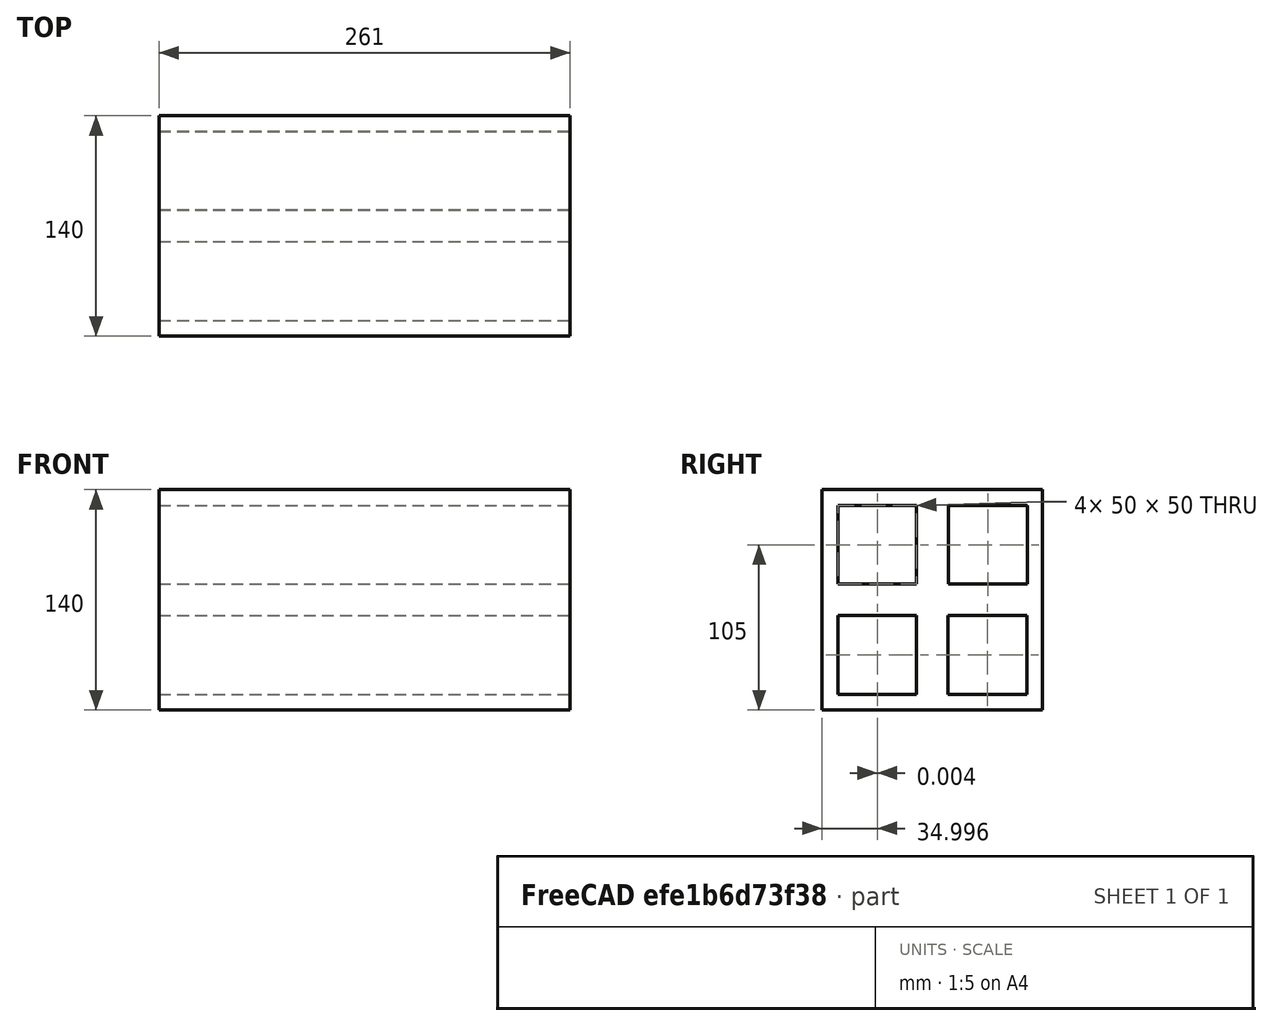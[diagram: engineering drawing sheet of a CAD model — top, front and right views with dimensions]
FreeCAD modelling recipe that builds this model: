
FCSTD DOCUMENT  (FreeCAD 0.21R33694 (Git))
Label: OJT1_T19R01_totxo
License: All rights reserved
LicenseURL: https://en.wikipedia.org/wiki/All_rights_reserved
objects: Sketcher::SketchObject×1, PartDesign::Pad×1, PartDesign::Body×1
note: 4 computed .brp shape members not serialized (recipe doc carries the construction recipe); baked Part::Feature solids carry a one-line shape summary decoded from their .brp

FEATURE [Sketcher::SketchObject] Sketch
  FullyConstrained = false
  MapMode = 5
  Placement = pos=(0,0,0) rot=(0.57735,0.57735,0.57735;2.0944rad)
  Support = -> [YZ_Plane]
  sketch-geometry (20):
    g0: LineSegment StartX=-70 StartY=70 StartZ=0 EndX=70 EndY=70 EndZ=0
    g1: LineSegment StartX=70 StartY=70 StartZ=0 EndX=70 EndY=-70 EndZ=0
    g2: LineSegment StartX=70 StartY=-70 StartZ=0 EndX=-70 EndY=-70 EndZ=0
    g3: LineSegment StartX=-70 StartY=-70 StartZ=0 EndX=-70 EndY=70 EndZ=0
    g4: LineSegment StartX=-60.0035 StartY=60 StartZ=0 EndX=-10.0035 EndY=60 EndZ=0
    g5: LineSegment StartX=-10.0035 StartY=60 StartZ=0 EndX=-10.0035 EndY=10 EndZ=0
    g6: LineSegment StartX=-10.0035 StartY=10 StartZ=0 EndX=-60.0035 EndY=10 EndZ=0
    g7: LineSegment StartX=-60.0035 StartY=10 StartZ=0 EndX=-60.0035 EndY=60 EndZ=0
    g8: LineSegment StartX=10.2823 StartY=60 StartZ=0 EndX=60.2823 EndY=60 EndZ=0
    g9: LineSegment StartX=60.2823 StartY=60 StartZ=0 EndX=60.2823 EndY=10 EndZ=0
    g10: LineSegment StartX=60.2823 StartY=10 StartZ=0 EndX=10.2823 EndY=10 EndZ=0
    g11: LineSegment StartX=10.2823 StartY=10 StartZ=0 EndX=10.2823 EndY=60 EndZ=0
    g12: LineSegment StartX=-60 StartY=-10 StartZ=0 EndX=-10 EndY=-10 EndZ=0
    g13: LineSegment StartX=-10 StartY=-10 StartZ=0 EndX=-10 EndY=-60 EndZ=0
    g14: LineSegment StartX=-10 StartY=-60 StartZ=0 EndX=-60 EndY=-60 EndZ=0
    g15: LineSegment StartX=-60 StartY=-60 StartZ=0 EndX=-60 EndY=-10 EndZ=0
    g16: LineSegment StartX=10 StartY=-10 StartZ=0 EndX=60 EndY=-10 EndZ=0
    g17: LineSegment StartX=60 StartY=-10 StartZ=0 EndX=60 EndY=-60 EndZ=0
    g18: LineSegment StartX=60 StartY=-60 StartZ=0 EndX=10 EndY=-60 EndZ=0
    g19: LineSegment StartX=10 StartY=-60 StartZ=0 EndX=10 EndY=-10 EndZ=0
  constraints (56):
    c: Coincident(g0,g1)
    c: Coincident(g1,g2)
    c: Coincident(g2,g3)
    c: Coincident(g3,g0)
    c: Horizontal(g2)
    c: Vertical(g1)
    c: Symmetric(g0,g0,g-2)
    c: Symmetric(g0,g2,g-1)
    c: DistanceX(g0,g0) = 140
    c: DistanceY(g3,g3) = 140
    c: Coincident(g4,g5)
    c: Coincident(g5,g6)
    c: Coincident(g6,g7)
    c: Coincident(g7,g4)
    c: Horizontal(g4)
    c: Horizontal(g6)
    c: Vertical(g5)
    c: Vertical(g7)
    c: DistanceX(g4,g4) = 50
    c: DistanceY(g5,g5) = 50
    c: DistanceY(g4,g0) = 10
    c: Coincident(g8,g9)
    c: Coincident(g9,g10)
    c: Coincident(g10,g11)
    c: Coincident(g11,g8)
    c: Horizontal(g8)
    c: Horizontal(g10)
    c: Vertical(g9)
    c: Vertical(g11)
    c: DistanceX(g8,g8) = 50
    c: DistanceY(g11,g11) = 50
    c: DistanceY(g8,g0) = 10
    c: Coincident(g12,g13)
    c: Coincident(g13,g14)
    c: Coincident(g14,g15)
    c: Coincident(g15,g12)
    c: Horizontal(g12)
    c: Horizontal(g14)
    c: Vertical(g13)
    c: Vertical(g15)
    c: Coincident(g16,g17)
    c: Coincident(g17,g18)
    c: Coincident(g18,g19)
    c: Coincident(g19,g16)
    c: Horizontal(g16)
    c: Horizontal(g18)
    c: Vertical(g17)
    c: Vertical(g19)
    c: DistanceY(g13,g13) = 50
    c: DistanceX(g12,g12) = 50
    c: DistanceX(g16,g16) = 50
    c: DistanceY(g17,g17) = 50
    c: DistanceY(g1,g17) = 10
    c: DistanceX(g17,g1) = 10
    c: DistanceX(g2,g14) = 10
    c: DistanceY(g2,g14) = 10
FEATURE [PartDesign::Pad] Pad
  Direction = (1,-2e-16,3e-16)
  Length = 261
  Length2 = 10
  Placement = pos=(0,0,0) rot=(1,1,1;2.0944rad)
  Profile = -> Sketch
  ReferenceAxis = -> Sketch [N_Axis]
  Type = 0
FEATURE [PartDesign::Body] Body
  Group = -> [Sketch,Pad]
  Origin = -> Origin
  Tip = -> Pad
